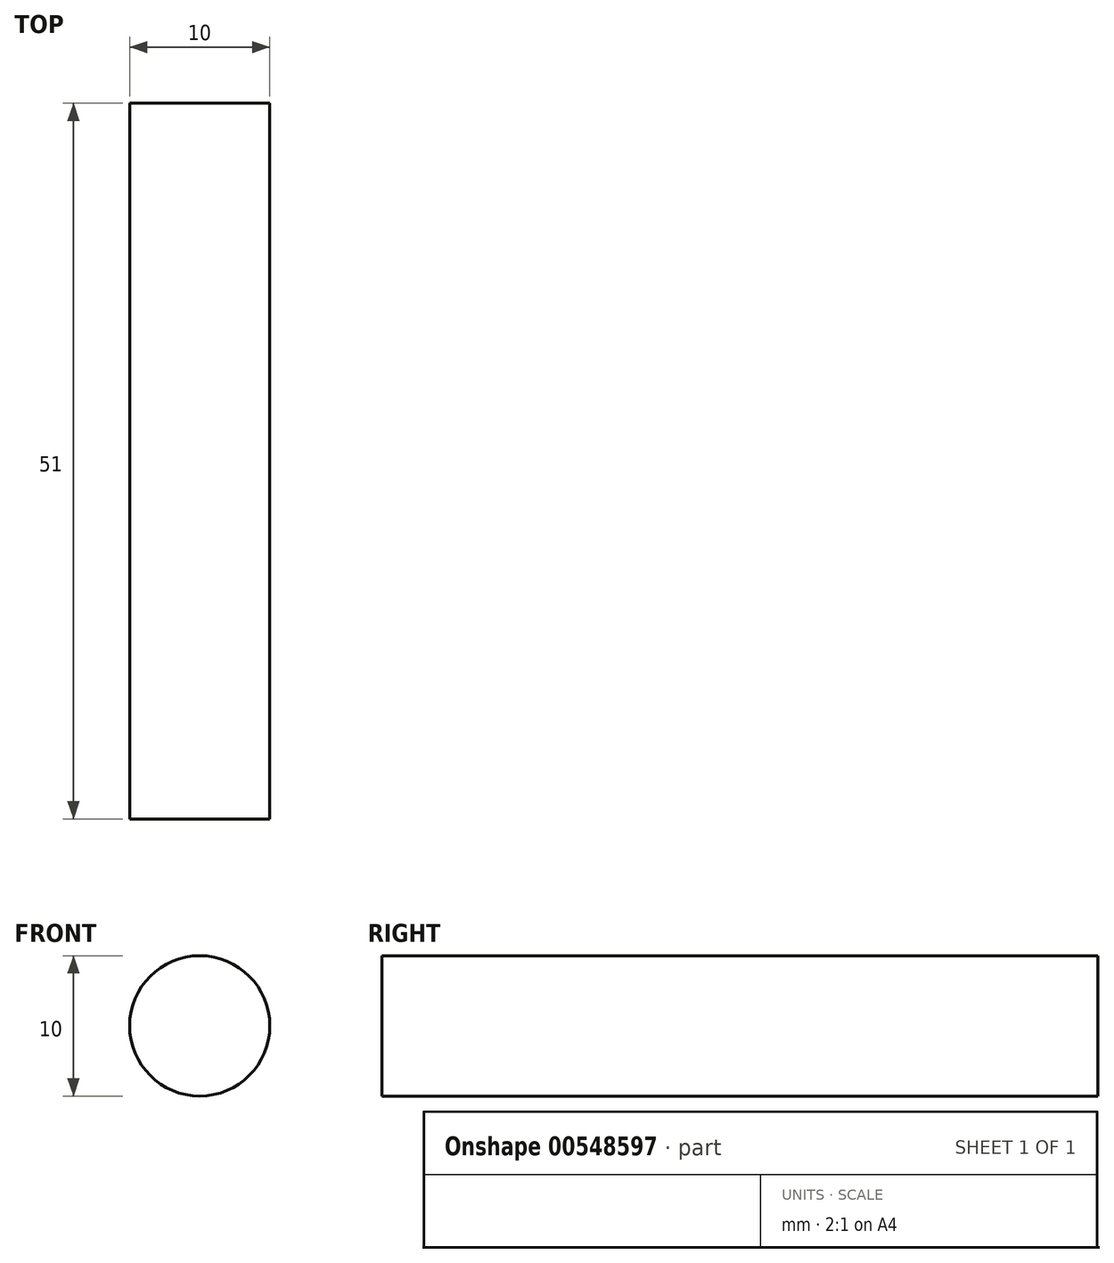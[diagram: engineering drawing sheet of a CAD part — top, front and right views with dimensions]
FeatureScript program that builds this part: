
annotation { "Feature Type Name" : "Feature", "Feature Type Description" : "" }
export const myFeature = defineFeature(function(context is Context, id is Id, definition is map)
    precondition{}
    {
        {
            var Q0;
            Q0=qCreatedBy(makeId("Front.planeOp"),FACE);
            var sketch = newSketch(context, id + "F0", { "sketchPlane" : qUnion([Q0])});
            skCircle(sketch, "E0", {"center": v(0, 0) * mm, "radius": 5 * mm});
            skSolve(sketch);
        }
        {
            var Q0;
            Q0=qSketchRegion(id+"F0",true);
            extrude(context, id + "F1", {"entities" : qUnion([Q0]), "endBound" : BoundingType.SYMMETRIC, "depth" : 51 * mm, "offsetDistance" : 25 * mm});
        }
    });
